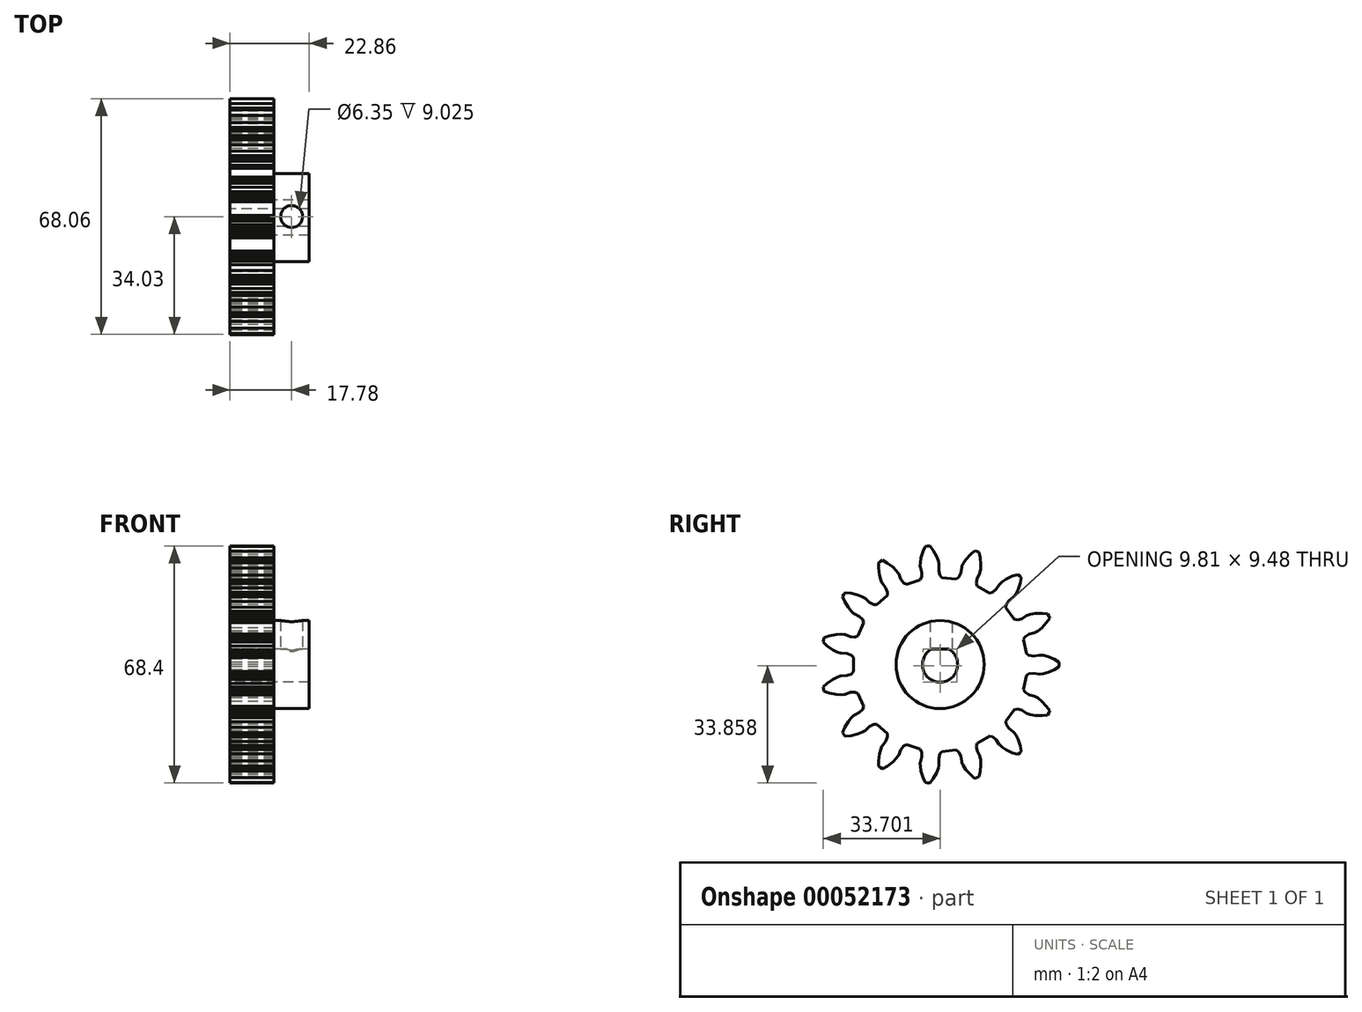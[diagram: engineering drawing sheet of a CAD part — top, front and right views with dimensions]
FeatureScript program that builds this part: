
annotation { "Feature Type Name" : "Feature", "Feature Type Description" : "" }
export const myFeature = defineFeature(function(context is Context, id is Id, definition is map)
    precondition{}
    {
        {
            var Q0;
            Q0=qCreatedBy(makeId("Right.planeOp"),FACE);
            var sketch = newSketch(context, id + "F0", { "sketchPlane" : qUnion([Q0])});
            skLineSegment(sketch, "E0", {"start": v(30.75, -14.57) * mm, "end": v(31.06, -13.98) * mm});
            skLineSegment(sketch, "E1", {"start": v(31.06, -13.98) * mm, "end": v(31.3, -13.35) * mm});
            skLineSegment(sketch, "E2", {"start": v(31.3, -13.35) * mm, "end": v(30.37, -12.04) * mm});
            skLineSegment(sketch, "E3", {"start": v(30.37, -12.04) * mm, "end": v(29.02, -10.6) * mm});
            skLineSegment(sketch, "E4", {"start": v(29.02, -10.6) * mm, "end": v(27.9, -9.7) * mm});
            skLineSegment(sketch, "E5", {"start": v(27.9, -9.7) * mm, "end": v(27.17, -9.26) * mm});
            skLineSegment(sketch, "E6", {"start": v(27.17, -9.26) * mm, "end": v(26.89, -9.14) * mm});
            skLineSegment(sketch, "E7", {"start": v(26.89, -9.14) * mm, "end": v(25.35, -8.73) * mm});
            skLineSegment(sketch, "E8", {"start": v(25.35, -8.73) * mm, "end": v(24.18, -8) * mm});
            skLineSegment(sketch, "E9", {"start": v(24.18, -8) * mm, "end": v(23.7, -7.19) * mm});
            skLineSegment(sketch, "E10", {"start": v(23.7, -7.19) * mm, "end": v(24.55, -3.2) * mm});
            skLineSegment(sketch, "E11", {"start": v(24.55, -3.2) * mm, "end": v(25.31, -2.66) * mm});
            skLineSegment(sketch, "E12", {"start": v(25.31, -2.66) * mm, "end": v(26.68, -2.47) * mm});
            skLineSegment(sketch, "E13", {"start": v(26.68, -2.47) * mm, "end": v(28.25, -2.72) * mm});
            skLineSegment(sketch, "E14", {"start": v(28.25, -2.72) * mm, "end": v(28.56, -2.73) * mm});
            skLineSegment(sketch, "E15", {"start": v(28.56, -2.73) * mm, "end": v(29.41, -2.62) * mm});
            skLineSegment(sketch, "E16", {"start": v(29.41, -2.62) * mm, "end": v(30.79, -2.26) * mm});
            skLineSegment(sketch, "E17", {"start": v(30.79, -2.26) * mm, "end": v(32.61, -1.49) * mm});
            skLineSegment(sketch, "E18", {"start": v(32.61, -1.49) * mm, "end": v(33.99, -0.67) * mm});
            skLineSegment(sketch, "E19", {"start": v(33.99, -0.67) * mm, "end": v(34.03, 0) * mm});
            skLineSegment(sketch, "E20", {"start": v(34.03, 0) * mm, "end": v(33.99, 0.67) * mm});
            skLineSegment(sketch, "E21", {"start": v(33.99, 0.67) * mm, "end": v(32.61, 1.49) * mm});
            skLineSegment(sketch, "E22", {"start": v(32.61, 1.49) * mm, "end": v(30.79, 2.26) * mm});
            skLineSegment(sketch, "E23", {"start": v(30.79, 2.26) * mm, "end": v(29.41, 2.62) * mm});
            skLineSegment(sketch, "E24", {"start": v(29.41, 2.62) * mm, "end": v(28.56, 2.73) * mm});
            skLineSegment(sketch, "E25", {"start": v(28.56, 2.73) * mm, "end": v(28.25, 2.72) * mm});
            skLineSegment(sketch, "E26", {"start": v(28.25, 2.72) * mm, "end": v(26.68, 2.47) * mm});
            skLineSegment(sketch, "E27", {"start": v(26.68, 2.47) * mm, "end": v(25.31, 2.66) * mm});
            skLineSegment(sketch, "E28", {"start": v(25.31, 2.66) * mm, "end": v(24.55, 3.2) * mm});
            skLineSegment(sketch, "E29", {"start": v(24.55, 3.2) * mm, "end": v(23.7, 7.19) * mm});
            skLineSegment(sketch, "E30", {"start": v(23.7, 7.19) * mm, "end": v(24.18, 8) * mm});
            skLineSegment(sketch, "E31", {"start": v(24.18, 8) * mm, "end": v(25.35, 8.73) * mm});
            skLineSegment(sketch, "E32", {"start": v(25.35, 8.73) * mm, "end": v(26.89, 9.14) * mm});
            skLineSegment(sketch, "E33", {"start": v(26.89, 9.14) * mm, "end": v(27.17, 9.26) * mm});
            skLineSegment(sketch, "E34", {"start": v(27.17, 9.26) * mm, "end": v(27.9, 9.7) * mm});
            skLineSegment(sketch, "E35", {"start": v(27.9, 9.7) * mm, "end": v(29.02, 10.6) * mm});
            skLineSegment(sketch, "E36", {"start": v(29.02, 10.6) * mm, "end": v(30.37, 12.04) * mm});
            skLineSegment(sketch, "E37", {"start": v(30.37, 12.04) * mm, "end": v(31.3, 13.35) * mm});
            skLineSegment(sketch, "E38", {"start": v(31.3, 13.35) * mm, "end": v(31.06, 13.98) * mm});
            skLineSegment(sketch, "E39", {"start": v(31.06, 13.98) * mm, "end": v(30.75, 14.57) * mm});
            skLineSegment(sketch, "E40", {"start": v(30.75, 14.57) * mm, "end": v(29.16, 14.76) * mm});
            skLineSegment(sketch, "E41", {"start": v(29.16, 14.76) * mm, "end": v(27.18, 14.72) * mm});
            skLineSegment(sketch, "E42", {"start": v(27.18, 14.72) * mm, "end": v(25.77, 14.5) * mm});
            skLineSegment(sketch, "E43", {"start": v(25.77, 14.5) * mm, "end": v(24.95, 14.24) * mm});
            skLineSegment(sketch, "E44", {"start": v(24.95, 14.24) * mm, "end": v(24.68, 14.11) * mm});
            skLineSegment(sketch, "E45", {"start": v(24.68, 14.11) * mm, "end": v(23.34, 13.24) * mm});
            skLineSegment(sketch, "E46", {"start": v(23.34, 13.24) * mm, "end": v(22.01, 12.86) * mm});
            skLineSegment(sketch, "E47", {"start": v(22.01, 12.86) * mm, "end": v(21.1, 13.05) * mm});
            skLineSegment(sketch, "E48", {"start": v(21.1, 13.05) * mm, "end": v(18.7, 16.34) * mm});
            skLineSegment(sketch, "E49", {"start": v(18.7, 16.34) * mm, "end": v(18.8, 17.27) * mm});
            skLineSegment(sketch, "E50", {"start": v(18.8, 17.27) * mm, "end": v(19.58, 18.42) * mm});
            skLineSegment(sketch, "E51", {"start": v(19.58, 18.42) * mm, "end": v(20.82, 19.42) * mm});
            skLineSegment(sketch, "E52", {"start": v(20.82, 19.42) * mm, "end": v(21.02, 19.64) * mm});
            skLineSegment(sketch, "E53", {"start": v(21.02, 19.64) * mm, "end": v(21.52, 20.35) * mm});
            skLineSegment(sketch, "E54", {"start": v(21.52, 20.35) * mm, "end": v(22.17, 21.61) * mm});
            skLineSegment(sketch, "E55", {"start": v(22.17, 21.61) * mm, "end": v(22.82, 23.49) * mm});
            skLineSegment(sketch, "E56", {"start": v(22.82, 23.49) * mm, "end": v(23.13, 25.05) * mm});
            skLineSegment(sketch, "E57", {"start": v(23.13, 25.05) * mm, "end": v(22.66, 25.54) * mm});
            skLineSegment(sketch, "E58", {"start": v(22.66, 25.54) * mm, "end": v(22.14, 25.95) * mm});
            skLineSegment(sketch, "E59", {"start": v(22.14, 25.95) * mm, "end": v(20.6, 25.48) * mm});
            skLineSegment(sketch, "E60", {"start": v(20.6, 25.48) * mm, "end": v(18.81, 24.63) * mm});
            skLineSegment(sketch, "E61", {"start": v(18.81, 24.63) * mm, "end": v(17.62, 23.86) * mm});
            skLineSegment(sketch, "E62", {"start": v(17.62, 23.86) * mm, "end": v(16.97, 23.29) * mm});
            skLineSegment(sketch, "E63", {"start": v(16.97, 23.29) * mm, "end": v(16.77, 23.06) * mm});
            skLineSegment(sketch, "E64", {"start": v(16.77, 23.06) * mm, "end": v(15.9, 21.72) * mm});
            skLineSegment(sketch, "E65", {"start": v(15.9, 21.72) * mm, "end": v(14.85, 20.84) * mm});
            skLineSegment(sketch, "E66", {"start": v(14.85, 20.84) * mm, "end": v(13.94, 20.64) * mm});
            skLineSegment(sketch, "E67", {"start": v(13.94, 20.64) * mm, "end": v(10.41, 22.67) * mm});
            skLineSegment(sketch, "E68", {"start": v(10.41, 22.67) * mm, "end": v(10.13, 23.56) * mm});
            skLineSegment(sketch, "E69", {"start": v(10.13, 23.56) * mm, "end": v(10.37, 24.92) * mm});
            skLineSegment(sketch, "E70", {"start": v(10.37, 24.92) * mm, "end": v(11.1, 26.34) * mm});
            skLineSegment(sketch, "E71", {"start": v(11.1, 26.34) * mm, "end": v(11.2, 26.63) * mm});
            skLineSegment(sketch, "E72", {"start": v(11.2, 26.63) * mm, "end": v(11.36, 27.47) * mm});
            skLineSegment(sketch, "E73", {"start": v(11.36, 27.47) * mm, "end": v(11.43, 28.9) * mm});
            skLineSegment(sketch, "E74", {"start": v(11.43, 28.9) * mm, "end": v(11.27, 30.87) * mm});
            skLineSegment(sketch, "E75", {"start": v(11.27, 30.87) * mm, "end": v(10.9, 32.43) * mm});
            skLineSegment(sketch, "E76", {"start": v(10.9, 32.43) * mm, "end": v(10.29, 32.68) * mm});
            skLineSegment(sketch, "E77", {"start": v(10.29, 32.68) * mm, "end": v(9.64, 32.84) * mm});
            skLineSegment(sketch, "E78", {"start": v(9.64, 32.84) * mm, "end": v(8.44, 31.8) * mm});
            skLineSegment(sketch, "E79", {"start": v(8.44, 31.8) * mm, "end": v(7.14, 30.3) * mm});
            skLineSegment(sketch, "E80", {"start": v(7.14, 30.3) * mm, "end": v(6.37, 29.1) * mm});
            skLineSegment(sketch, "E81", {"start": v(6.37, 29.1) * mm, "end": v(6, 28.31) * mm});
            skLineSegment(sketch, "E82", {"start": v(6, 28.31) * mm, "end": v(5.92, 28.02) * mm});
            skLineSegment(sketch, "E83", {"start": v(5.92, 28.02) * mm, "end": v(5.67, 26.45) * mm});
            skLineSegment(sketch, "E84", {"start": v(5.67, 26.45) * mm, "end": v(5.06, 25.2) * mm});
            skLineSegment(sketch, "E85", {"start": v(5.06, 25.2) * mm, "end": v(4.3, 24.66) * mm});
            skLineSegment(sketch, "E86", {"start": v(4.3, 24.66) * mm, "end": v(0.26, 25.08) * mm});
            skLineSegment(sketch, "E87", {"start": v(0.26, 25.08) * mm, "end": v(-0.36, 25.78) * mm});
            skLineSegment(sketch, "E88", {"start": v(-0.36, 25.78) * mm, "end": v(-0.7, 27.12) * mm});
            skLineSegment(sketch, "E89", {"start": v(-0.7, 27.12) * mm, "end": v(-0.61, 28.7) * mm});
            skLineSegment(sketch, "E90", {"start": v(-0.61, 28.7) * mm, "end": v(-0.64, 29.01) * mm});
            skLineSegment(sketch, "E91", {"start": v(-0.64, 29.01) * mm, "end": v(-0.83, 29.85) * mm});
            skLineSegment(sketch, "E92", {"start": v(-0.83, 29.85) * mm, "end": v(-1.34, 31.18) * mm});
            skLineSegment(sketch, "E93", {"start": v(-1.34, 31.18) * mm, "end": v(-2.3, 32.92) * mm});
            skLineSegment(sketch, "E94", {"start": v(-2.3, 32.92) * mm, "end": v(-3.25, 34.2) * mm});
            skLineSegment(sketch, "E95", {"start": v(-3.25, 34.2) * mm, "end": v(-3.92, 34.17) * mm});
            skLineSegment(sketch, "E96", {"start": v(-3.92, 34.17) * mm, "end": v(-4.58, 34.06) * mm});
            skLineSegment(sketch, "E97", {"start": v(-4.58, 34.06) * mm, "end": v(-5.25, 32.6) * mm});
            skLineSegment(sketch, "E98", {"start": v(-5.25, 32.6) * mm, "end": v(-5.83, 30.7) * mm});
            skLineSegment(sketch, "E99", {"start": v(-5.83, 30.7) * mm, "end": v(-6.05, 29.3) * mm});
            skLineSegment(sketch, "E100", {"start": v(-6.05, 29.3) * mm, "end": v(-6.06, 28.44) * mm});
            skLineSegment(sketch, "E101", {"start": v(-6.06, 28.44) * mm, "end": v(-6.02, 28.14) * mm});
            skLineSegment(sketch, "E102", {"start": v(-6.02, 28.14) * mm, "end": v(-5.6, 26.6) * mm});
            skLineSegment(sketch, "E103", {"start": v(-5.6, 26.6) * mm, "end": v(-5.66, 25.22) * mm});
            skLineSegment(sketch, "E104", {"start": v(-5.66, 25.22) * mm, "end": v(-6.12, 24.41) * mm});
            skLineSegment(sketch, "E105", {"start": v(-6.12, 24.41) * mm, "end": v(-10, 23.15) * mm});
            skLineSegment(sketch, "E106", {"start": v(-10, 23.15) * mm, "end": v(-10.84, 23.54) * mm});
            skLineSegment(sketch, "E107", {"start": v(-10.84, 23.54) * mm, "end": v(-11.7, 24.62) * mm});
            skLineSegment(sketch, "E108", {"start": v(-11.7, 24.62) * mm, "end": v(-12.26, 26.11) * mm});
            skLineSegment(sketch, "E109", {"start": v(-12.26, 26.11) * mm, "end": v(-12.4, 26.38) * mm});
            skLineSegment(sketch, "E110", {"start": v(-12.4, 26.38) * mm, "end": v(-12.93, 27.07) * mm});
            skLineSegment(sketch, "E111", {"start": v(-12.93, 27.07) * mm, "end": v(-13.93, 28.08) * mm});
            skLineSegment(sketch, "E112", {"start": v(-13.93, 28.08) * mm, "end": v(-15.51, 29.27) * mm});
            skLineSegment(sketch, "E113", {"start": v(-15.51, 29.27) * mm, "end": v(-16.9, 30.05) * mm});
            skLineSegment(sketch, "E114", {"start": v(-16.9, 30.05) * mm, "end": v(-17.5, 29.76) * mm});
            skLineSegment(sketch, "E115", {"start": v(-17.5, 29.76) * mm, "end": v(-18.06, 29.38) * mm});
            skLineSegment(sketch, "E116", {"start": v(-18.06, 29.38) * mm, "end": v(-18.09, 27.79) * mm});
            skLineSegment(sketch, "E117", {"start": v(-18.09, 27.79) * mm, "end": v(-17.84, 25.82) * mm});
            skLineSegment(sketch, "E118", {"start": v(-17.84, 25.82) * mm, "end": v(-17.47, 24.44) * mm});
            skLineSegment(sketch, "E119", {"start": v(-17.47, 24.44) * mm, "end": v(-17.13, 23.65) * mm});
            skLineSegment(sketch, "E120", {"start": v(-17.13, 23.65) * mm, "end": v(-16.98, 23.4) * mm});
            skLineSegment(sketch, "E121", {"start": v(-16.98, 23.4) * mm, "end": v(-15.97, 22.16) * mm});
            skLineSegment(sketch, "E122", {"start": v(-15.97, 22.16) * mm, "end": v(-15.46, 20.87) * mm});
            skLineSegment(sketch, "E123", {"start": v(-15.46, 20.87) * mm, "end": v(-15.55, 19.94) * mm});
            skLineSegment(sketch, "E124", {"start": v(-15.55, 19.94) * mm, "end": v(-18.57, 17.22) * mm});
            skLineSegment(sketch, "E125", {"start": v(-18.57, 17.22) * mm, "end": v(-19.5, 17.23) * mm});
            skLineSegment(sketch, "E126", {"start": v(-19.5, 17.23) * mm, "end": v(-20.73, 17.87) * mm});
            skLineSegment(sketch, "E127", {"start": v(-20.73, 17.87) * mm, "end": v(-21.85, 19) * mm});
            skLineSegment(sketch, "E128", {"start": v(-21.85, 19) * mm, "end": v(-22.1, 19.18) * mm});
            skLineSegment(sketch, "E129", {"start": v(-22.1, 19.18) * mm, "end": v(-22.85, 19.6) * mm});
            skLineSegment(sketch, "E130", {"start": v(-22.85, 19.6) * mm, "end": v(-24.18, 20.12) * mm});
            skLineSegment(sketch, "E131", {"start": v(-24.18, 20.12) * mm, "end": v(-26.1, 20.57) * mm});
            skLineSegment(sketch, "E132", {"start": v(-26.1, 20.57) * mm, "end": v(-27.7, 20.7) * mm});
            skLineSegment(sketch, "E133", {"start": v(-27.7, 20.7) * mm, "end": v(-28.13, 20.2) * mm});
            skLineSegment(sketch, "E134", {"start": v(-28.13, 20.2) * mm, "end": v(-28.48, 19.63) * mm});
            skLineSegment(sketch, "E135", {"start": v(-28.48, 19.63) * mm, "end": v(-27.85, 18.16) * mm});
            skLineSegment(sketch, "E136", {"start": v(-27.85, 18.16) * mm, "end": v(-26.83, 16.46) * mm});
            skLineSegment(sketch, "E137", {"start": v(-26.83, 16.46) * mm, "end": v(-25.93, 15.36) * mm});
            skLineSegment(sketch, "E138", {"start": v(-25.93, 15.36) * mm, "end": v(-25.3, 14.77) * mm});
            skLineSegment(sketch, "E139", {"start": v(-25.3, 14.77) * mm, "end": v(-25.05, 14.6) * mm});
            skLineSegment(sketch, "E140", {"start": v(-25.05, 14.6) * mm, "end": v(-23.63, 13.88) * mm});
            skLineSegment(sketch, "E141", {"start": v(-23.63, 13.88) * mm, "end": v(-22.64, 12.92) * mm});
            skLineSegment(sketch, "E142", {"start": v(-22.64, 12.92) * mm, "end": v(-22.35, 12.03) * mm});
            skLineSegment(sketch, "E143", {"start": v(-22.35, 12.03) * mm, "end": v(-24, 8.31) * mm});
            skLineSegment(sketch, "E144", {"start": v(-24, 8.31) * mm, "end": v(-24.86, 7.94) * mm});
            skLineSegment(sketch, "E145", {"start": v(-24.86, 7.94) * mm, "end": v(-26.23, 8.03) * mm});
            skLineSegment(sketch, "E146", {"start": v(-26.23, 8.03) * mm, "end": v(-27.72, 8.6) * mm});
            skLineSegment(sketch, "E147", {"start": v(-27.72, 8.6) * mm, "end": v(-28.02, 8.67) * mm});
            skLineSegment(sketch, "E148", {"start": v(-28.02, 8.67) * mm, "end": v(-28.87, 8.75) * mm});
            skLineSegment(sketch, "E149", {"start": v(-28.87, 8.75) * mm, "end": v(-30.3, 8.68) * mm});
            skLineSegment(sketch, "E150", {"start": v(-30.3, 8.68) * mm, "end": v(-32.24, 8.3) * mm});
            skLineSegment(sketch, "E151", {"start": v(-32.24, 8.3) * mm, "end": v(-33.76, 7.79) * mm});
            skLineSegment(sketch, "E152", {"start": v(-33.76, 7.79) * mm, "end": v(-33.94, 7.14) * mm});
            skLineSegment(sketch, "E153", {"start": v(-33.94, 7.14) * mm, "end": v(-34.03, 6.48) * mm});
            skLineSegment(sketch, "E154", {"start": v(-34.03, 6.48) * mm, "end": v(-32.86, 5.4) * mm});
            skLineSegment(sketch, "E155", {"start": v(-32.86, 5.4) * mm, "end": v(-31.23, 4.26) * mm});
            skLineSegment(sketch, "E156", {"start": v(-31.23, 4.26) * mm, "end": v(-29.97, 3.62) * mm});
            skLineSegment(sketch, "E157", {"start": v(-29.97, 3.62) * mm, "end": v(-29.15, 3.34) * mm});
            skLineSegment(sketch, "E158", {"start": v(-29.15, 3.34) * mm, "end": v(-28.85, 3.28) * mm});
            skLineSegment(sketch, "E159", {"start": v(-28.85, 3.28) * mm, "end": v(-27.26, 3.2) * mm});
            skLineSegment(sketch, "E160", {"start": v(-27.26, 3.2) * mm, "end": v(-25.96, 2.73) * mm});
            skLineSegment(sketch, "E161", {"start": v(-25.96, 2.73) * mm, "end": v(-25.34, 2.03) * mm});
            skLineSegment(sketch, "E162", {"start": v(-25.34, 2.03) * mm, "end": v(-25.34, -2.03) * mm});
            skLineSegment(sketch, "E163", {"start": v(-25.34, -2.03) * mm, "end": v(-25.96, -2.73) * mm});
            skLineSegment(sketch, "E164", {"start": v(-25.96, -2.73) * mm, "end": v(-27.26, -3.2) * mm});
            skLineSegment(sketch, "E165", {"start": v(-27.26, -3.2) * mm, "end": v(-28.85, -3.28) * mm});
            skLineSegment(sketch, "E166", {"start": v(-28.85, -3.28) * mm, "end": v(-29.15, -3.34) * mm});
            skLineSegment(sketch, "E167", {"start": v(-29.15, -3.34) * mm, "end": v(-29.97, -3.62) * mm});
            skLineSegment(sketch, "E168", {"start": v(-29.97, -3.62) * mm, "end": v(-31.23, -4.26) * mm});
            skLineSegment(sketch, "E169", {"start": v(-31.23, -4.26) * mm, "end": v(-32.86, -5.4) * mm});
            skLineSegment(sketch, "E170", {"start": v(-32.86, -5.4) * mm, "end": v(-34.03, -6.48) * mm});
            skLineSegment(sketch, "E171", {"start": v(-34.03, -6.48) * mm, "end": v(-33.94, -7.14) * mm});
            skLineSegment(sketch, "E172", {"start": v(-33.94, -7.14) * mm, "end": v(-33.76, -7.79) * mm});
            skLineSegment(sketch, "E173", {"start": v(-33.76, -7.79) * mm, "end": v(-32.24, -8.3) * mm});
            skLineSegment(sketch, "E174", {"start": v(-32.24, -8.3) * mm, "end": v(-30.3, -8.68) * mm});
            skLineSegment(sketch, "E175", {"start": v(-30.3, -8.68) * mm, "end": v(-28.87, -8.75) * mm});
            skLineSegment(sketch, "E176", {"start": v(-28.87, -8.75) * mm, "end": v(-28.02, -8.67) * mm});
            skLineSegment(sketch, "E177", {"start": v(-28.02, -8.67) * mm, "end": v(-27.72, -8.6) * mm});
            skLineSegment(sketch, "E178", {"start": v(-27.72, -8.6) * mm, "end": v(-26.23, -8.03) * mm});
            skLineSegment(sketch, "E179", {"start": v(-26.23, -8.03) * mm, "end": v(-24.86, -7.94) * mm});
            skLineSegment(sketch, "E180", {"start": v(-24.86, -7.94) * mm, "end": v(-24, -8.31) * mm});
            skLineSegment(sketch, "E181", {"start": v(-24, -8.31) * mm, "end": v(-22.35, -12.03) * mm});
            skLineSegment(sketch, "E182", {"start": v(-22.35, -12.03) * mm, "end": v(-22.64, -12.92) * mm});
            skLineSegment(sketch, "E183", {"start": v(-22.64, -12.92) * mm, "end": v(-23.63, -13.88) * mm});
            skLineSegment(sketch, "E184", {"start": v(-23.63, -13.88) * mm, "end": v(-25.05, -14.6) * mm});
            skLineSegment(sketch, "E185", {"start": v(-25.05, -14.6) * mm, "end": v(-25.3, -14.77) * mm});
            skLineSegment(sketch, "E186", {"start": v(-25.3, -14.77) * mm, "end": v(-25.93, -15.36) * mm});
            skLineSegment(sketch, "E187", {"start": v(-25.93, -15.36) * mm, "end": v(-26.83, -16.46) * mm});
            skLineSegment(sketch, "E188", {"start": v(-26.83, -16.46) * mm, "end": v(-27.85, -18.16) * mm});
            skLineSegment(sketch, "E189", {"start": v(-27.85, -18.16) * mm, "end": v(-28.48, -19.63) * mm});
            skLineSegment(sketch, "E190", {"start": v(-28.48, -19.63) * mm, "end": v(-28.13, -20.2) * mm});
            skLineSegment(sketch, "E191", {"start": v(-28.13, -20.2) * mm, "end": v(-27.7, -20.7) * mm});
            skLineSegment(sketch, "E192", {"start": v(-27.7, -20.7) * mm, "end": v(-26.1, -20.57) * mm});
            skLineSegment(sketch, "E193", {"start": v(-26.1, -20.57) * mm, "end": v(-24.18, -20.12) * mm});
            skLineSegment(sketch, "E194", {"start": v(-24.18, -20.12) * mm, "end": v(-22.85, -19.6) * mm});
            skLineSegment(sketch, "E195", {"start": v(-22.85, -19.6) * mm, "end": v(-22.1, -19.18) * mm});
            skLineSegment(sketch, "E196", {"start": v(-22.1, -19.18) * mm, "end": v(-21.85, -19) * mm});
            skLineSegment(sketch, "E197", {"start": v(-21.85, -19) * mm, "end": v(-20.73, -17.87) * mm});
            skLineSegment(sketch, "E198", {"start": v(-20.73, -17.87) * mm, "end": v(-19.5, -17.23) * mm});
            skLineSegment(sketch, "E199", {"start": v(-19.5, -17.23) * mm, "end": v(-18.57, -17.22) * mm});
            skLineSegment(sketch, "E200", {"start": v(-18.57, -17.22) * mm, "end": v(-15.55, -19.94) * mm});
            skLineSegment(sketch, "E201", {"start": v(-15.55, -19.94) * mm, "end": v(-15.46, -20.87) * mm});
            skLineSegment(sketch, "E202", {"start": v(-15.46, -20.87) * mm, "end": v(-15.97, -22.16) * mm});
            skLineSegment(sketch, "E203", {"start": v(-15.97, -22.16) * mm, "end": v(-16.98, -23.4) * mm});
            skLineSegment(sketch, "E204", {"start": v(-16.98, -23.4) * mm, "end": v(-17.13, -23.65) * mm});
            skLineSegment(sketch, "E205", {"start": v(-17.13, -23.65) * mm, "end": v(-17.47, -24.44) * mm});
            skLineSegment(sketch, "E206", {"start": v(-17.47, -24.44) * mm, "end": v(-17.84, -25.82) * mm});
            skLineSegment(sketch, "E207", {"start": v(-17.84, -25.82) * mm, "end": v(-18.09, -27.79) * mm});
            skLineSegment(sketch, "E208", {"start": v(-18.09, -27.79) * mm, "end": v(-18.06, -29.38) * mm});
            skLineSegment(sketch, "E209", {"start": v(-18.06, -29.38) * mm, "end": v(-17.5, -29.76) * mm});
            skLineSegment(sketch, "E210", {"start": v(-17.5, -29.76) * mm, "end": v(-16.9, -30.05) * mm});
            skLineSegment(sketch, "E211", {"start": v(-16.9, -30.05) * mm, "end": v(-15.51, -29.27) * mm});
            skLineSegment(sketch, "E212", {"start": v(-15.51, -29.27) * mm, "end": v(-13.93, -28.08) * mm});
            skLineSegment(sketch, "E213", {"start": v(-13.93, -28.08) * mm, "end": v(-12.93, -27.07) * mm});
            skLineSegment(sketch, "E214", {"start": v(-12.93, -27.07) * mm, "end": v(-12.4, -26.38) * mm});
            skLineSegment(sketch, "E215", {"start": v(-12.4, -26.38) * mm, "end": v(-12.26, -26.11) * mm});
            skLineSegment(sketch, "E216", {"start": v(-12.26, -26.11) * mm, "end": v(-11.7, -24.62) * mm});
            skLineSegment(sketch, "E217", {"start": v(-11.7, -24.62) * mm, "end": v(-10.84, -23.54) * mm});
            skLineSegment(sketch, "E218", {"start": v(-10.84, -23.54) * mm, "end": v(-10, -23.15) * mm});
            skLineSegment(sketch, "E219", {"start": v(-10, -23.15) * mm, "end": v(-6.12, -24.41) * mm});
            skLineSegment(sketch, "E220", {"start": v(-6.12, -24.41) * mm, "end": v(-5.66, -25.22) * mm});
            skLineSegment(sketch, "E221", {"start": v(-5.66, -25.22) * mm, "end": v(-5.6, -26.6) * mm});
            skLineSegment(sketch, "E222", {"start": v(-5.6, -26.6) * mm, "end": v(-6.02, -28.14) * mm});
            skLineSegment(sketch, "E223", {"start": v(-6.02, -28.14) * mm, "end": v(-6.06, -28.44) * mm});
            skLineSegment(sketch, "E224", {"start": v(-6.06, -28.44) * mm, "end": v(-6.05, -29.3) * mm});
            skLineSegment(sketch, "E225", {"start": v(-6.05, -29.3) * mm, "end": v(-5.83, -30.7) * mm});
            skLineSegment(sketch, "E226", {"start": v(-5.83, -30.7) * mm, "end": v(-5.25, -32.6) * mm});
            skLineSegment(sketch, "E227", {"start": v(-5.25, -32.6) * mm, "end": v(-4.58, -34.06) * mm});
            skLineSegment(sketch, "E228", {"start": v(-4.58, -34.06) * mm, "end": v(-3.92, -34.17) * mm});
            skLineSegment(sketch, "E229", {"start": v(-3.92, -34.17) * mm, "end": v(-3.25, -34.2) * mm});
            skLineSegment(sketch, "E230", {"start": v(-3.25, -34.2) * mm, "end": v(-2.3, -32.92) * mm});
            skLineSegment(sketch, "E231", {"start": v(-2.3, -32.92) * mm, "end": v(-1.34, -31.18) * mm});
            skLineSegment(sketch, "E232", {"start": v(-1.34, -31.18) * mm, "end": v(-0.83, -29.85) * mm});
            skLineSegment(sketch, "E233", {"start": v(-0.83, -29.85) * mm, "end": v(-0.64, -29.01) * mm});
            skLineSegment(sketch, "E234", {"start": v(-0.64, -29.01) * mm, "end": v(-0.61, -28.7) * mm});
            skLineSegment(sketch, "E235", {"start": v(-0.61, -28.7) * mm, "end": v(-0.7, -27.12) * mm});
            skLineSegment(sketch, "E236", {"start": v(-0.7, -27.12) * mm, "end": v(-0.36, -25.78) * mm});
            skLineSegment(sketch, "E237", {"start": v(-0.36, -25.78) * mm, "end": v(0.26, -25.08) * mm});
            skLineSegment(sketch, "E238", {"start": v(0.26, -25.08) * mm, "end": v(4.3, -24.66) * mm});
            skLineSegment(sketch, "E239", {"start": v(4.3, -24.66) * mm, "end": v(5.06, -25.2) * mm});
            skLineSegment(sketch, "E240", {"start": v(5.06, -25.2) * mm, "end": v(5.67, -26.45) * mm});
            skLineSegment(sketch, "E241", {"start": v(5.67, -26.45) * mm, "end": v(5.92, -28.02) * mm});
            skLineSegment(sketch, "E242", {"start": v(5.92, -28.02) * mm, "end": v(6, -28.31) * mm});
            skLineSegment(sketch, "E243", {"start": v(6, -28.31) * mm, "end": v(6.37, -29.1) * mm});
            skLineSegment(sketch, "E244", {"start": v(6.37, -29.1) * mm, "end": v(7.14, -30.3) * mm});
            skLineSegment(sketch, "E245", {"start": v(7.14, -30.3) * mm, "end": v(8.44, -31.8) * mm});
            skLineSegment(sketch, "E246", {"start": v(8.44, -31.8) * mm, "end": v(9.64, -32.84) * mm});
            skLineSegment(sketch, "E247", {"start": v(9.64, -32.84) * mm, "end": v(10.29, -32.68) * mm});
            skLineSegment(sketch, "E248", {"start": v(10.29, -32.68) * mm, "end": v(10.9, -32.43) * mm});
            skLineSegment(sketch, "E249", {"start": v(10.9, -32.43) * mm, "end": v(11.27, -30.87) * mm});
            skLineSegment(sketch, "E250", {"start": v(11.27, -30.87) * mm, "end": v(11.43, -28.9) * mm});
            skLineSegment(sketch, "E251", {"start": v(11.43, -28.9) * mm, "end": v(11.36, -27.47) * mm});
            skLineSegment(sketch, "E252", {"start": v(11.36, -27.47) * mm, "end": v(11.2, -26.63) * mm});
            skLineSegment(sketch, "E253", {"start": v(11.2, -26.63) * mm, "end": v(11.1, -26.34) * mm});
            skLineSegment(sketch, "E254", {"start": v(11.1, -26.34) * mm, "end": v(10.37, -24.92) * mm});
            skLineSegment(sketch, "E255", {"start": v(10.37, -24.92) * mm, "end": v(10.13, -23.56) * mm});
            skLineSegment(sketch, "E256", {"start": v(10.13, -23.56) * mm, "end": v(10.41, -22.67) * mm});
            skLineSegment(sketch, "E257", {"start": v(10.41, -22.67) * mm, "end": v(13.94, -20.64) * mm});
            skLineSegment(sketch, "E258", {"start": v(13.94, -20.64) * mm, "end": v(14.85, -20.84) * mm});
            skLineSegment(sketch, "E259", {"start": v(14.85, -20.84) * mm, "end": v(15.9, -21.72) * mm});
            skLineSegment(sketch, "E260", {"start": v(15.9, -21.72) * mm, "end": v(16.77, -23.06) * mm});
            skLineSegment(sketch, "E261", {"start": v(16.77, -23.06) * mm, "end": v(16.97, -23.29) * mm});
            skLineSegment(sketch, "E262", {"start": v(16.97, -23.29) * mm, "end": v(17.62, -23.86) * mm});
            skLineSegment(sketch, "E263", {"start": v(17.62, -23.86) * mm, "end": v(18.81, -24.63) * mm});
            skLineSegment(sketch, "E264", {"start": v(18.81, -24.63) * mm, "end": v(20.6, -25.48) * mm});
            skLineSegment(sketch, "E265", {"start": v(20.6, -25.48) * mm, "end": v(22.14, -25.95) * mm});
            skLineSegment(sketch, "E266", {"start": v(22.14, -25.95) * mm, "end": v(22.66, -25.54) * mm});
            skLineSegment(sketch, "E267", {"start": v(22.66, -25.54) * mm, "end": v(23.13, -25.05) * mm});
            skLineSegment(sketch, "E268", {"start": v(23.13, -25.05) * mm, "end": v(22.82, -23.49) * mm});
            skLineSegment(sketch, "E269", {"start": v(22.82, -23.49) * mm, "end": v(22.17, -21.61) * mm});
            skLineSegment(sketch, "E270", {"start": v(22.17, -21.61) * mm, "end": v(21.52, -20.35) * mm});
            skLineSegment(sketch, "E271", {"start": v(21.52, -20.35) * mm, "end": v(21.02, -19.64) * mm});
            skLineSegment(sketch, "E272", {"start": v(21.02, -19.64) * mm, "end": v(20.82, -19.42) * mm});
            skLineSegment(sketch, "E273", {"start": v(20.82, -19.42) * mm, "end": v(19.58, -18.42) * mm});
            skLineSegment(sketch, "E274", {"start": v(19.58, -18.42) * mm, "end": v(18.8, -17.27) * mm});
            skLineSegment(sketch, "E275", {"start": v(18.8, -17.27) * mm, "end": v(18.7, -16.34) * mm});
            skLineSegment(sketch, "E276", {"start": v(18.7, -16.34) * mm, "end": v(21.1, -13.05) * mm});
            skLineSegment(sketch, "E277", {"start": v(21.1, -13.05) * mm, "end": v(22.01, -12.86) * mm});
            skLineSegment(sketch, "E278", {"start": v(22.01, -12.86) * mm, "end": v(23.34, -13.24) * mm});
            skLineSegment(sketch, "E279", {"start": v(23.34, -13.24) * mm, "end": v(24.68, -14.11) * mm});
            skLineSegment(sketch, "E280", {"start": v(24.68, -14.11) * mm, "end": v(24.95, -14.24) * mm});
            skLineSegment(sketch, "E281", {"start": v(24.95, -14.24) * mm, "end": v(25.77, -14.5) * mm});
            skLineSegment(sketch, "E282", {"start": v(25.77, -14.5) * mm, "end": v(27.18, -14.72) * mm});
            skLineSegment(sketch, "E283", {"start": v(27.18, -14.72) * mm, "end": v(29.16, -14.76) * mm});
            skLineSegment(sketch, "E284", {"start": v(29.16, -14.76) * mm, "end": v(30.75, -14.57) * mm});
            skArc(sketch, "E285", {"start": v(-2.88, 4.4) * mm, "mid": v(-0.33, -5.08) * mm, "end": v(2.22, 4.4) * mm});
            skPoint(sketch, "E286.orphan", {"position": v(5.99, -0.66) * mm});
            skPoint(sketch, "E287.start.orphan", {"position": v(5.99, 0.66) * mm});
            skPoint(sketch, "E288.orphan", {"position": v(5.99, 0) * mm});
            skPoint(sketch, "E289.orphan", {"position": v(-0.33, 6.35) * mm});
            skPoint(sketch, "E290.orphan", {"position": v(-6.64, 0.66) * mm});
            skPoint(sketch, "E291.end.orphan", {"position": v(-6.64, 0) * mm});
            skPoint(sketch, "E291.start.orphan", {"position": v(-6.64, -0.66) * mm});
            skPoint(sketch, "E292.end.orphan", {"position": v(-0.33, -6.35) * mm});
            skLineSegment(sketch, "E293", {"start": v(-2.88, 4.4) * mm, "end": v(2.22, 4.4) * mm});
            skSolve(sketch);
        }
        {
            var Q0;
            Q0=makeQuery(id+"F0.imprint","IMPRINT",FACE,{"disambiguationData":[TD([[makeQuery(id+"F0.imprint","IMPRINT",EDGE,{"derivedFrom":sQuery(id+"F0.wireOp",EDGE,"E0")}),1.0]])]});
            extrude(context, id + "F1", {"entities" : qUnion([Q0]), "depth" : 12.7 * mm});
        }
        {
            var Q0;
            Q0=makeQuery(id+"F1.opExtrude","CAP_FACE",FACE,{"disambiguationData":[OSD([sQuery(id+"F0.wireOp",EDGE,"E0"),sQuery(id+"F0.wireOp",EDGE,"E1"),sQuery(id+"F0.wireOp",EDGE,"E2"),sQuery(id+"F0.wireOp",EDGE,"E3"),sQuery(id+"F0.wireOp",EDGE,"E4"),sQuery(id+"F0.wireOp",EDGE,"E5"),sQuery(id+"F0.wireOp",EDGE,"E6"),sQuery(id+"F0.wireOp",EDGE,"E7"),sQuery(id+"F0.wireOp",EDGE,"E8"),sQuery(id+"F0.wireOp",EDGE,"E9"),sQuery(id+"F0.wireOp",EDGE,"E10"),sQuery(id+"F0.wireOp",EDGE,"E11"),sQuery(id+"F0.wireOp",EDGE,"E12"),sQuery(id+"F0.wireOp",EDGE,"E13"),sQuery(id+"F0.wireOp",EDGE,"E14"),sQuery(id+"F0.wireOp",EDGE,"E15"),sQuery(id+"F0.wireOp",EDGE,"E16"),sQuery(id+"F0.wireOp",EDGE,"E17"),sQuery(id+"F0.wireOp",EDGE,"E18"),sQuery(id+"F0.wireOp",EDGE,"E19"),sQuery(id+"F0.wireOp",EDGE,"E20"),sQuery(id+"F0.wireOp",EDGE,"E21"),sQuery(id+"F0.wireOp",EDGE,"E22"),sQuery(id+"F0.wireOp",EDGE,"E23"),sQuery(id+"F0.wireOp",EDGE,"E24"),sQuery(id+"F0.wireOp",EDGE,"E25"),sQuery(id+"F0.wireOp",EDGE,"E26"),sQuery(id+"F0.wireOp",EDGE,"E27"),sQuery(id+"F0.wireOp",EDGE,"E28"),sQuery(id+"F0.wireOp",EDGE,"E29"),sQuery(id+"F0.wireOp",EDGE,"E30"),sQuery(id+"F0.wireOp",EDGE,"E31"),sQuery(id+"F0.wireOp",EDGE,"E32"),sQuery(id+"F0.wireOp",EDGE,"E33"),sQuery(id+"F0.wireOp",EDGE,"E34"),sQuery(id+"F0.wireOp",EDGE,"E35"),sQuery(id+"F0.wireOp",EDGE,"E36"),sQuery(id+"F0.wireOp",EDGE,"E37"),sQuery(id+"F0.wireOp",EDGE,"E38"),sQuery(id+"F0.wireOp",EDGE,"E39"),sQuery(id+"F0.wireOp",EDGE,"E40"),sQuery(id+"F0.wireOp",EDGE,"E41"),sQuery(id+"F0.wireOp",EDGE,"E42"),sQuery(id+"F0.wireOp",EDGE,"E43"),sQuery(id+"F0.wireOp",EDGE,"E44"),sQuery(id+"F0.wireOp",EDGE,"E45"),sQuery(id+"F0.wireOp",EDGE,"E46"),sQuery(id+"F0.wireOp",EDGE,"E47"),sQuery(id+"F0.wireOp",EDGE,"E48"),sQuery(id+"F0.wireOp",EDGE,"E49"),sQuery(id+"F0.wireOp",EDGE,"E50"),sQuery(id+"F0.wireOp",EDGE,"E51"),sQuery(id+"F0.wireOp",EDGE,"E52"),sQuery(id+"F0.wireOp",EDGE,"E53"),sQuery(id+"F0.wireOp",EDGE,"E54"),sQuery(id+"F0.wireOp",EDGE,"E55"),sQuery(id+"F0.wireOp",EDGE,"E56"),sQuery(id+"F0.wireOp",EDGE,"E57"),sQuery(id+"F0.wireOp",EDGE,"E58"),sQuery(id+"F0.wireOp",EDGE,"E59"),sQuery(id+"F0.wireOp",EDGE,"E60"),sQuery(id+"F0.wireOp",EDGE,"E61"),sQuery(id+"F0.wireOp",EDGE,"E62"),sQuery(id+"F0.wireOp",EDGE,"E63"),sQuery(id+"F0.wireOp",EDGE,"E64"),sQuery(id+"F0.wireOp",EDGE,"E65"),sQuery(id+"F0.wireOp",EDGE,"E66"),sQuery(id+"F0.wireOp",EDGE,"E67"),sQuery(id+"F0.wireOp",EDGE,"E68"),sQuery(id+"F0.wireOp",EDGE,"E69"),sQuery(id+"F0.wireOp",EDGE,"E70"),sQuery(id+"F0.wireOp",EDGE,"E71"),sQuery(id+"F0.wireOp",EDGE,"E72"),sQuery(id+"F0.wireOp",EDGE,"E73"),sQuery(id+"F0.wireOp",EDGE,"E74"),sQuery(id+"F0.wireOp",EDGE,"E75"),sQuery(id+"F0.wireOp",EDGE,"E76"),sQuery(id+"F0.wireOp",EDGE,"E77"),sQuery(id+"F0.wireOp",EDGE,"E78"),sQuery(id+"F0.wireOp",EDGE,"E79"),sQuery(id+"F0.wireOp",EDGE,"E80"),sQuery(id+"F0.wireOp",EDGE,"E81"),sQuery(id+"F0.wireOp",EDGE,"E82"),sQuery(id+"F0.wireOp",EDGE,"E83"),sQuery(id+"F0.wireOp",EDGE,"E84"),sQuery(id+"F0.wireOp",EDGE,"E85"),sQuery(id+"F0.wireOp",EDGE,"E86"),sQuery(id+"F0.wireOp",EDGE,"E87"),sQuery(id+"F0.wireOp",EDGE,"E88"),sQuery(id+"F0.wireOp",EDGE,"E89"),sQuery(id+"F0.wireOp",EDGE,"E90"),sQuery(id+"F0.wireOp",EDGE,"E91"),sQuery(id+"F0.wireOp",EDGE,"E92"),sQuery(id+"F0.wireOp",EDGE,"E93"),sQuery(id+"F0.wireOp",EDGE,"E94"),sQuery(id+"F0.wireOp",EDGE,"E95"),sQuery(id+"F0.wireOp",EDGE,"E96"),sQuery(id+"F0.wireOp",EDGE,"E97"),sQuery(id+"F0.wireOp",EDGE,"E98"),sQuery(id+"F0.wireOp",EDGE,"E99"),sQuery(id+"F0.wireOp",EDGE,"E100"),sQuery(id+"F0.wireOp",EDGE,"E101"),sQuery(id+"F0.wireOp",EDGE,"E102"),sQuery(id+"F0.wireOp",EDGE,"E103"),sQuery(id+"F0.wireOp",EDGE,"E104"),sQuery(id+"F0.wireOp",EDGE,"E105"),sQuery(id+"F0.wireOp",EDGE,"E106"),sQuery(id+"F0.wireOp",EDGE,"E107"),sQuery(id+"F0.wireOp",EDGE,"E108"),sQuery(id+"F0.wireOp",EDGE,"E109"),sQuery(id+"F0.wireOp",EDGE,"E110"),sQuery(id+"F0.wireOp",EDGE,"E111"),sQuery(id+"F0.wireOp",EDGE,"E112"),sQuery(id+"F0.wireOp",EDGE,"E113"),sQuery(id+"F0.wireOp",EDGE,"E114"),sQuery(id+"F0.wireOp",EDGE,"E115"),sQuery(id+"F0.wireOp",EDGE,"E116"),sQuery(id+"F0.wireOp",EDGE,"E117"),sQuery(id+"F0.wireOp",EDGE,"E118"),sQuery(id+"F0.wireOp",EDGE,"E119"),sQuery(id+"F0.wireOp",EDGE,"E120"),sQuery(id+"F0.wireOp",EDGE,"E121"),sQuery(id+"F0.wireOp",EDGE,"E122"),sQuery(id+"F0.wireOp",EDGE,"E123"),sQuery(id+"F0.wireOp",EDGE,"E124"),sQuery(id+"F0.wireOp",EDGE,"E125"),sQuery(id+"F0.wireOp",EDGE,"E126"),sQuery(id+"F0.wireOp",EDGE,"E127"),sQuery(id+"F0.wireOp",EDGE,"E128"),sQuery(id+"F0.wireOp",EDGE,"E129"),sQuery(id+"F0.wireOp",EDGE,"E130"),sQuery(id+"F0.wireOp",EDGE,"E131"),sQuery(id+"F0.wireOp",EDGE,"E132"),sQuery(id+"F0.wireOp",EDGE,"E133"),sQuery(id+"F0.wireOp",EDGE,"E134"),sQuery(id+"F0.wireOp",EDGE,"E135"),sQuery(id+"F0.wireOp",EDGE,"E136"),sQuery(id+"F0.wireOp",EDGE,"E137"),sQuery(id+"F0.wireOp",EDGE,"E138"),sQuery(id+"F0.wireOp",EDGE,"E139"),sQuery(id+"F0.wireOp",EDGE,"E140"),sQuery(id+"F0.wireOp",EDGE,"E141"),sQuery(id+"F0.wireOp",EDGE,"E142"),sQuery(id+"F0.wireOp",EDGE,"E143"),sQuery(id+"F0.wireOp",EDGE,"E144"),sQuery(id+"F0.wireOp",EDGE,"E145"),sQuery(id+"F0.wireOp",EDGE,"E146"),sQuery(id+"F0.wireOp",EDGE,"E147"),sQuery(id+"F0.wireOp",EDGE,"E148"),sQuery(id+"F0.wireOp",EDGE,"E149"),sQuery(id+"F0.wireOp",EDGE,"E150"),sQuery(id+"F0.wireOp",EDGE,"E151"),sQuery(id+"F0.wireOp",EDGE,"E152"),sQuery(id+"F0.wireOp",EDGE,"E153"),sQuery(id+"F0.wireOp",EDGE,"E154"),sQuery(id+"F0.wireOp",EDGE,"E155"),sQuery(id+"F0.wireOp",EDGE,"E156"),sQuery(id+"F0.wireOp",EDGE,"E157"),sQuery(id+"F0.wireOp",EDGE,"E158"),sQuery(id+"F0.wireOp",EDGE,"E159"),sQuery(id+"F0.wireOp",EDGE,"E160"),sQuery(id+"F0.wireOp",EDGE,"E161"),sQuery(id+"F0.wireOp",EDGE,"E162"),sQuery(id+"F0.wireOp",EDGE,"E163"),sQuery(id+"F0.wireOp",EDGE,"E164"),sQuery(id+"F0.wireOp",EDGE,"E165"),sQuery(id+"F0.wireOp",EDGE,"E166"),sQuery(id+"F0.wireOp",EDGE,"E167"),sQuery(id+"F0.wireOp",EDGE,"E168"),sQuery(id+"F0.wireOp",EDGE,"E169"),sQuery(id+"F0.wireOp",EDGE,"E170"),sQuery(id+"F0.wireOp",EDGE,"E171"),sQuery(id+"F0.wireOp",EDGE,"E172"),sQuery(id+"F0.wireOp",EDGE,"E173"),sQuery(id+"F0.wireOp",EDGE,"E174"),sQuery(id+"F0.wireOp",EDGE,"E175"),sQuery(id+"F0.wireOp",EDGE,"E176"),sQuery(id+"F0.wireOp",EDGE,"E177"),sQuery(id+"F0.wireOp",EDGE,"E178"),sQuery(id+"F0.wireOp",EDGE,"E179"),sQuery(id+"F0.wireOp",EDGE,"E180"),sQuery(id+"F0.wireOp",EDGE,"E181"),sQuery(id+"F0.wireOp",EDGE,"E182"),sQuery(id+"F0.wireOp",EDGE,"E183"),sQuery(id+"F0.wireOp",EDGE,"E184"),sQuery(id+"F0.wireOp",EDGE,"E185"),sQuery(id+"F0.wireOp",EDGE,"E186"),sQuery(id+"F0.wireOp",EDGE,"E187"),sQuery(id+"F0.wireOp",EDGE,"E188"),sQuery(id+"F0.wireOp",EDGE,"E189"),sQuery(id+"F0.wireOp",EDGE,"E190"),sQuery(id+"F0.wireOp",EDGE,"E191"),sQuery(id+"F0.wireOp",EDGE,"E192"),sQuery(id+"F0.wireOp",EDGE,"E193"),sQuery(id+"F0.wireOp",EDGE,"E194"),sQuery(id+"F0.wireOp",EDGE,"E195"),sQuery(id+"F0.wireOp",EDGE,"E196"),sQuery(id+"F0.wireOp",EDGE,"E197"),sQuery(id+"F0.wireOp",EDGE,"E198"),sQuery(id+"F0.wireOp",EDGE,"E199"),sQuery(id+"F0.wireOp",EDGE,"E200"),sQuery(id+"F0.wireOp",EDGE,"E201"),sQuery(id+"F0.wireOp",EDGE,"E202"),sQuery(id+"F0.wireOp",EDGE,"E203"),sQuery(id+"F0.wireOp",EDGE,"E204"),sQuery(id+"F0.wireOp",EDGE,"E205"),sQuery(id+"F0.wireOp",EDGE,"E206"),sQuery(id+"F0.wireOp",EDGE,"E207"),sQuery(id+"F0.wireOp",EDGE,"E208"),sQuery(id+"F0.wireOp",EDGE,"E209"),sQuery(id+"F0.wireOp",EDGE,"E210"),sQuery(id+"F0.wireOp",EDGE,"E211"),sQuery(id+"F0.wireOp",EDGE,"E212"),sQuery(id+"F0.wireOp",EDGE,"E213"),sQuery(id+"F0.wireOp",EDGE,"E214"),sQuery(id+"F0.wireOp",EDGE,"E215"),sQuery(id+"F0.wireOp",EDGE,"E216"),sQuery(id+"F0.wireOp",EDGE,"E217"),sQuery(id+"F0.wireOp",EDGE,"E218"),sQuery(id+"F0.wireOp",EDGE,"E219"),sQuery(id+"F0.wireOp",EDGE,"E220"),sQuery(id+"F0.wireOp",EDGE,"E221"),sQuery(id+"F0.wireOp",EDGE,"E222"),sQuery(id+"F0.wireOp",EDGE,"E223"),sQuery(id+"F0.wireOp",EDGE,"E224"),sQuery(id+"F0.wireOp",EDGE,"E225"),sQuery(id+"F0.wireOp",EDGE,"E226"),sQuery(id+"F0.wireOp",EDGE,"E227"),sQuery(id+"F0.wireOp",EDGE,"E228"),sQuery(id+"F0.wireOp",EDGE,"E229"),sQuery(id+"F0.wireOp",EDGE,"E230"),sQuery(id+"F0.wireOp",EDGE,"E231"),sQuery(id+"F0.wireOp",EDGE,"E232"),sQuery(id+"F0.wireOp",EDGE,"E233"),sQuery(id+"F0.wireOp",EDGE,"E234"),sQuery(id+"F0.wireOp",EDGE,"E235"),sQuery(id+"F0.wireOp",EDGE,"E236"),sQuery(id+"F0.wireOp",EDGE,"E237"),sQuery(id+"F0.wireOp",EDGE,"E238"),sQuery(id+"F0.wireOp",EDGE,"E239"),sQuery(id+"F0.wireOp",EDGE,"E240"),sQuery(id+"F0.wireOp",EDGE,"E241"),sQuery(id+"F0.wireOp",EDGE,"E242"),sQuery(id+"F0.wireOp",EDGE,"E243"),sQuery(id+"F0.wireOp",EDGE,"E244"),sQuery(id+"F0.wireOp",EDGE,"E245"),sQuery(id+"F0.wireOp",EDGE,"E246"),sQuery(id+"F0.wireOp",EDGE,"E247"),sQuery(id+"F0.wireOp",EDGE,"E248"),sQuery(id+"F0.wireOp",EDGE,"E249"),sQuery(id+"F0.wireOp",EDGE,"E250"),sQuery(id+"F0.wireOp",EDGE,"E251"),sQuery(id+"F0.wireOp",EDGE,"E252"),sQuery(id+"F0.wireOp",EDGE,"E253"),sQuery(id+"F0.wireOp",EDGE,"E254"),sQuery(id+"F0.wireOp",EDGE,"E255"),sQuery(id+"F0.wireOp",EDGE,"E256"),sQuery(id+"F0.wireOp",EDGE,"E257"),sQuery(id+"F0.wireOp",EDGE,"E258"),sQuery(id+"F0.wireOp",EDGE,"E259"),sQuery(id+"F0.wireOp",EDGE,"E260"),sQuery(id+"F0.wireOp",EDGE,"E261"),sQuery(id+"F0.wireOp",EDGE,"E262"),sQuery(id+"F0.wireOp",EDGE,"E263"),sQuery(id+"F0.wireOp",EDGE,"E264"),sQuery(id+"F0.wireOp",EDGE,"E265"),sQuery(id+"F0.wireOp",EDGE,"E266"),sQuery(id+"F0.wireOp",EDGE,"E267"),sQuery(id+"F0.wireOp",EDGE,"E268"),sQuery(id+"F0.wireOp",EDGE,"E269"),sQuery(id+"F0.wireOp",EDGE,"E270"),sQuery(id+"F0.wireOp",EDGE,"E271"),sQuery(id+"F0.wireOp",EDGE,"E272"),sQuery(id+"F0.wireOp",EDGE,"E273"),sQuery(id+"F0.wireOp",EDGE,"E274"),sQuery(id+"F0.wireOp",EDGE,"E275"),sQuery(id+"F0.wireOp",EDGE,"E276"),sQuery(id+"F0.wireOp",EDGE,"E277"),sQuery(id+"F0.wireOp",EDGE,"E278"),sQuery(id+"F0.wireOp",EDGE,"E279"),sQuery(id+"F0.wireOp",EDGE,"E280"),sQuery(id+"F0.wireOp",EDGE,"E281"),sQuery(id+"F0.wireOp",EDGE,"E282"),sQuery(id+"F0.wireOp",EDGE,"E283"),sQuery(id+"F0.wireOp",EDGE,"E284"),sQuery(id+"F0.wireOp",EDGE,"E285"),sQuery(id+"F0.wireOp",EDGE,"E293")])],"isStart":false});
            var sketch = newSketch(context, id + "F2", { "sketchPlane" : qUnion([Q0])});
            skArc(sketch, "E294", {"start": v(-2.88, 4.4) * mm, "mid": v(-0.33, -5.08) * mm, "end": v(2.22, 4.4) * mm});
            skPoint(sketch, "E294.first.point", {"position": v(-4.64, 2.69) * mm});
            skPoint(sketch, "E294.second.point", {"position": v(4.7, 0.68) * mm});
            skPoint(sketch, "E294.third.point", {"position": v(-0.33, -5.08) * mm});
            skCircle(sketch, "E295", {"center": v(-0.33, 0) * mm, "radius": 12.7 * mm});
            skLineSegment(sketch, "E296", {"start": v(-2.88, 4.4) * mm, "end": v(2.22, 4.4) * mm});
            skSolve(sketch);
        }
        {
            var Q0;
            Q0=makeQuery(id+"F2.imprint","IMPRINT",FACE,{"disambiguationData":[TD([[makeQuery(id+"F2.imprint","IMPRINT",EDGE,{"derivedFrom":sQuery(id+"F2.wireOp",EDGE,"E294")}),-1.0]])]});
            extrude(context, id + "F3", {"entities" : qUnion([Q0]), "operationType" : NewBodyOperationType.ADD, "depth" : 10.16 * mm});
        }
        {
            var Q0;
            Q0=qCreatedBy(makeId("Top.planeOp"),FACE);
            var sketch = newSketch(context, id + "F4", { "sketchPlane" : qUnion([Q0])});
            skCircle(sketch, "E297", {"center": v(17.78, 0) * mm, "radius": 3.17 * mm});
            skSolve(sketch);
        }
        {
            var Q0;
            Q0 = qSketchRegion(id + "F4", true);
            extrude(context, id + "F5", {"entities" : qUnion([Q0]), "operationType" : NewBodyOperationType.REMOVE, "depth" : 25.4 * mm});
        }
    });
